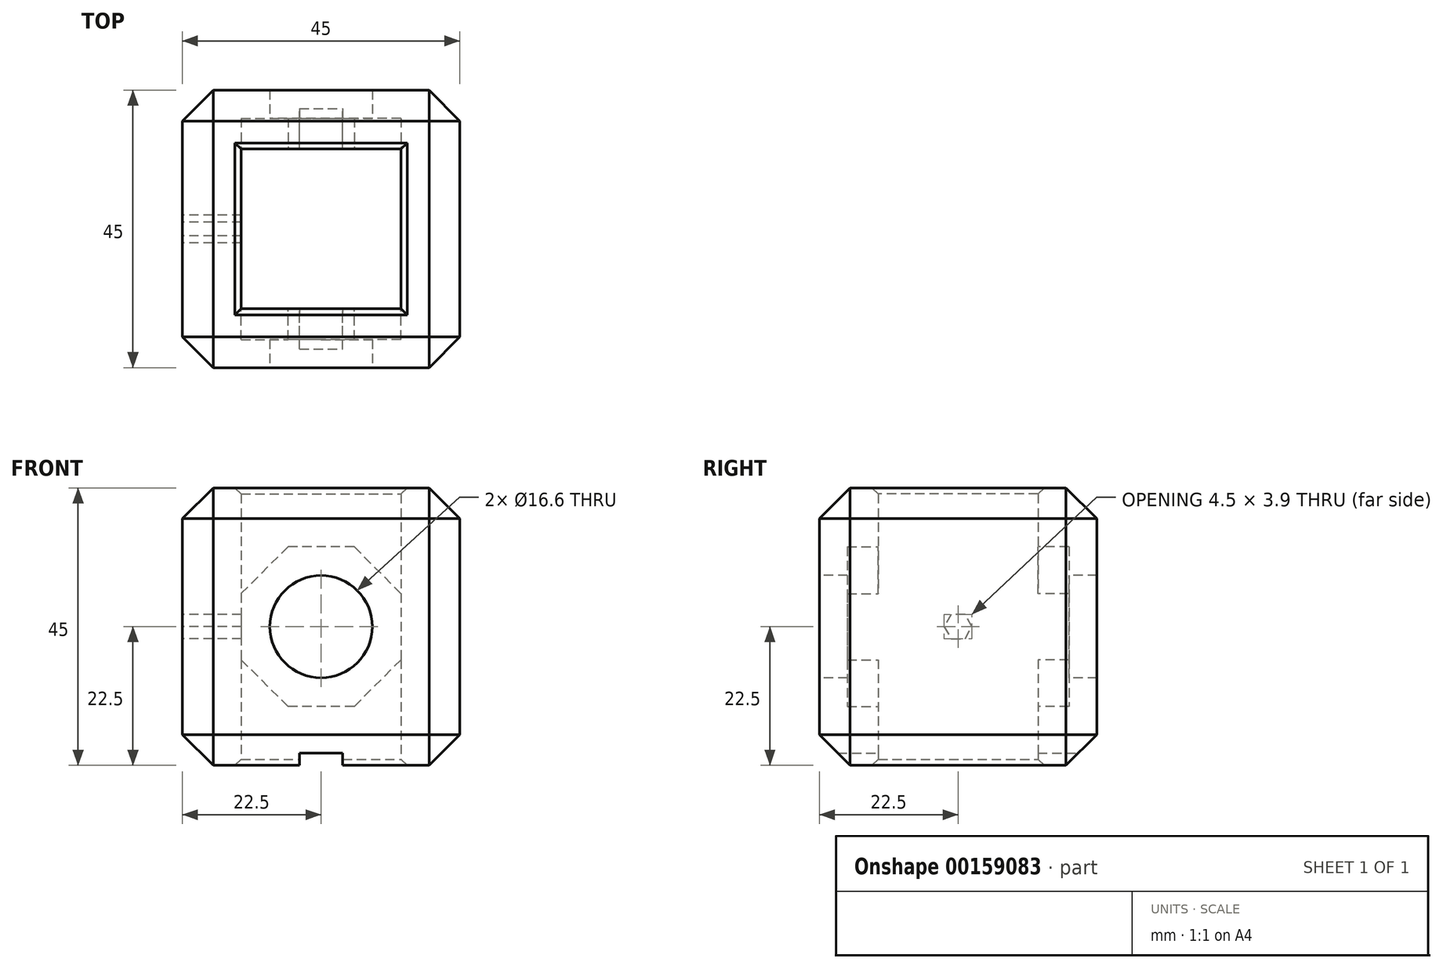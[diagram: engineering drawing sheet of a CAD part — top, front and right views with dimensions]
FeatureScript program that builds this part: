
annotation { "Feature Type Name" : "Feature", "Feature Type Description" : "" }
export const myFeature = defineFeature(function(context is Context, id is Id, definition is map)
    precondition{}
    {
        {
            var Q0;
            Q0=qCreatedBy(makeId("Top.planeOp"),FACE);
            var sketch = newSketch(context, id + "F0", { "sketchPlane" : qUnion([Q0])});
            skLineSegment(sketch, "E0.bottom", {"start": v(12.95, 12.95) * mm, "end": v(-12.95, 12.95) * mm});
            skLineSegment(sketch, "E0.top", {"start": v(12.95, -12.95) * mm, "end": v(-12.95, -12.95) * mm});
            skLineSegment(sketch, "E0.left", {"start": v(12.95, 12.95) * mm, "end": v(12.95, -12.95) * mm});
            skLineSegment(sketch, "E0.right", {"start": v(-12.95, 12.95) * mm, "end": v(-12.95, -12.95) * mm});
            skPoint(sketch, "E0.middle", {"position": v(0, 0) * mm});
            skLineSegment(sketch, "E1.bottom", {"start": v(22.5, -22.5) * mm, "end": v(-22.5, -22.5) * mm});
            skLineSegment(sketch, "E1.top", {"start": v(22.5, 22.5) * mm, "end": v(-22.5, 22.5) * mm});
            skLineSegment(sketch, "E1.left", {"start": v(22.5, -22.5) * mm, "end": v(22.5, 22.5) * mm});
            skLineSegment(sketch, "E1.right", {"start": v(-22.5, -22.5) * mm, "end": v(-22.5, 22.5) * mm});
            skSolve(sketch);
        }
        {
            var Q0;
            Q0=qSketchRegion(id+"F0",true);
            extrude(context, id + "F1", {"entities" : qUnion([Q0]), "depth" : 45 * mm});
        }
        {
            var Q0;
            Q0=makeQuery(id+"F1.opExtrude","SWEPT_FACE",FACE,{"disambiguationData":[OSD([sQuery(id+"F0.wireOp",EDGE,"E1.bottom")])]});
            var sketch = newSketch(context, id + "F2", { "sketchPlane" : qUnion([Q0])});
            skCircle(sketch, "E2", {"center": v(0, 22.5) * mm, "radius": 8.3 * mm});
            skSolve(sketch);
        }
        {
            var Q0;
            Q0=qSketchRegion(id+"F2",true);
            extrude(context, id + "F3", {"entities" : qUnion([Q0]), "operationType" : NewBodyOperationType.REMOVE, "endBound" : BoundingType.THROUGH_ALL, "oppositeDirection" : true, "depth" : 25 * mm});
        }
        {
            var Q0;
            Q0=makeQuery(id+"F1.opExtrude","SWEPT_FACE",FACE,{"disambiguationData":[OSD([sQuery(id+"F0.wireOp",EDGE,"E0.bottom")])]});
            var sketch = newSketch(context, id + "F4", { "sketchPlane" : qUnion([Q0])});
            skCircle(sketch, "E3.cCircle", {"center": v(0, 22.5) * mm, "radius": 12.95 * mm, "construction": true});
            skLineSegment(sketch, "E3.0", {"start": v(12.95, 27.86) * mm, "end": v(12.95, 17.14) * mm});
            skLineSegment(sketch, "E3.1", {"start": v(12.95, 17.14) * mm, "end": v(5.36, 9.55) * mm});
            skLineSegment(sketch, "E3.2", {"start": v(5.36, 9.55) * mm, "end": v(-5.36, 9.55) * mm});
            skLineSegment(sketch, "E3.3", {"start": v(-5.36, 9.55) * mm, "end": v(-12.95, 17.14) * mm});
            skLineSegment(sketch, "E3.4", {"start": v(-12.95, 17.14) * mm, "end": v(-12.95, 27.86) * mm});
            skLineSegment(sketch, "E3.5", {"start": v(-12.95, 27.86) * mm, "end": v(-5.36, 35.45) * mm});
            skLineSegment(sketch, "E3.6", {"start": v(-5.36, 35.45) * mm, "end": v(5.36, 35.45) * mm});
            skLineSegment(sketch, "E3.7", {"start": v(5.36, 35.45) * mm, "end": v(12.95, 27.86) * mm});
            skPoint(sketch, "E3.0.midPoint", {"position": v(12.95, 22.5) * mm});
            skSolve(sketch);
        }
        {
            var Q0;
            Q0=qSketchRegion(id+"F4",true);
            extrude(context, id + "F5", {"entities" : qUnion([Q0]), "operationType" : NewBodyOperationType.REMOVE, "oppositeDirection" : true, "depth" : 5 * mm});
        }
        {
            var Q0;
            Q0=makeQuery(id+"F1.opExtrude","SWEPT_FACE",FACE,{"disambiguationData":[OSD([sQuery(id+"F0.wireOp",EDGE,"E0.top")])]});
            var sketch = newSketch(context, id + "F6", { "sketchPlane" : qUnion([Q0])});
            skCircle(sketch, "E4.cCircle", {"center": v(0, 22.5) * mm, "radius": 12.95 * mm, "construction": true});
            skLineSegment(sketch, "E4.0", {"start": v(12.95, 27.86) * mm, "end": v(12.95, 17.14) * mm});
            skLineSegment(sketch, "E4.1", {"start": v(12.95, 17.14) * mm, "end": v(5.36, 9.55) * mm});
            skLineSegment(sketch, "E4.2", {"start": v(5.36, 9.55) * mm, "end": v(-5.36, 9.55) * mm});
            skLineSegment(sketch, "E4.3", {"start": v(-5.36, 9.55) * mm, "end": v(-12.95, 17.14) * mm});
            skLineSegment(sketch, "E4.4", {"start": v(-12.95, 17.14) * mm, "end": v(-12.95, 27.86) * mm});
            skLineSegment(sketch, "E4.5", {"start": v(-12.95, 27.86) * mm, "end": v(-5.36, 35.45) * mm});
            skLineSegment(sketch, "E4.6", {"start": v(-5.36, 35.45) * mm, "end": v(5.36, 35.45) * mm});
            skLineSegment(sketch, "E4.7", {"start": v(5.36, 35.45) * mm, "end": v(12.95, 27.86) * mm});
            skPoint(sketch, "E4.0.midPoint", {"position": v(12.95, 22.5) * mm});
            skSolve(sketch);
        }
        {
            var Q0;
            Q0=qSketchRegion(id+"F6",true);
            extrude(context, id + "F7", {"entities" : qUnion([Q0]), "operationType" : NewBodyOperationType.REMOVE, "oppositeDirection" : true, "depth" : 5 * mm});
        }
        {
            var Q0;
            Q0=makeQuery(id+"F1.opExtrude","SWEPT_FACE",FACE,{"disambiguationData":[OSD([sQuery(id+"F0.wireOp",EDGE,"E1.right")])]});
            var sketch = newSketch(context, id + "F8", { "sketchPlane" : qUnion([Q0])});
            skLineSegment(sketch, "E5", {"start": v(0, 45) * mm, "end": v(0, 0) * mm, "construction": true});
            skCircle(sketch, "E6.cCircle", {"center": v(0, 22.5) * mm, "radius": 1.95 * mm, "construction": true});
            skLineSegment(sketch, "E6.0", {"start": v(2.25, 22.5) * mm, "end": v(1.13, 20.55) * mm});
            skLineSegment(sketch, "E6.1", {"start": v(1.13, 20.55) * mm, "end": v(-1.13, 20.55) * mm});
            skLineSegment(sketch, "E6.2", {"start": v(-1.13, 20.55) * mm, "end": v(-2.25, 22.5) * mm});
            skLineSegment(sketch, "E6.3", {"start": v(-2.25, 22.5) * mm, "end": v(-1.13, 24.45) * mm});
            skLineSegment(sketch, "E6.4", {"start": v(-1.13, 24.45) * mm, "end": v(1.13, 24.45) * mm});
            skLineSegment(sketch, "E6.5", {"start": v(1.13, 24.45) * mm, "end": v(2.25, 22.5) * mm});
            skPoint(sketch, "E6.0.midPoint", {"position": v(1.69, 21.52) * mm});
            skSolve(sketch);
        }
        {
            var Q0;
            Q0=makeQuery(id+"F1.opExtrude","SWEPT_FACE",FACE,{"disambiguationData":[OSD([sQuery(id+"F0.wireOp",EDGE,"E1.left")])]});
            var Q1;
            Q1=makeQuery(id+"F1.opExtrude","SWEPT_FACE",FACE,{"disambiguationData":[OSD([sQuery(id+"F0.wireOp",EDGE,"E1.right")])]});
            var Q2;
            Q2=makeQuery(id+"F1.opExtrude","CAP_EDGE",EDGE,{"disambiguationData":[OSD([sQuery(id+"F0.wireOp",EDGE,"E1.bottom")])],"isStart":true});
            var Q3;
            Q3=makeQuery(id+"F1.opExtrude","CAP_EDGE",EDGE,{"disambiguationData":[OSD([sQuery(id+"F0.wireOp",EDGE,"E1.bottom")])],"isStart":false});
            var Q4;
            Q4=makeQuery(id+"F1.opExtrude","CAP_EDGE",EDGE,{"disambiguationData":[OSD([sQuery(id+"F0.wireOp",EDGE,"E1.top")])],"isStart":false});
            var Q5;
            Q5=makeQuery(id+"F1.opExtrude","CAP_EDGE",EDGE,{"disambiguationData":[OSD([sQuery(id+"F0.wireOp",EDGE,"E1.top")])],"isStart":true});
            chamfer(context, id + "F9", {"entities" : qUnion([Q0, Q1, Q2, Q3, Q4, Q5]), "width" : 5 * mm, "tangentPropagation" : true});
        }
        {
            var Q0;
            Q0 = qSketchRegion(id + "F8", true);
            extrude(context, id + "F10", {"entities" : qUnion([Q0]), "operationType" : NewBodyOperationType.REMOVE, "endBound" : BoundingType.UP_TO_NEXT, "oppositeDirection" : true, "depth" : 25 * mm});
        }
        {
            var Q0;
            Q0=makeQuery(id+"F5.boolean.opBoolean","INTERSECT",EDGE,{"derivedFrom":[makeQuery(id+"F3.boolean.opBoolean","COPY",FACE,{"disambiguationData":[TD([makeQuery(id+"F1.opExtrude","SWEPT_FACE",FACE,{"disambiguationData":[OSD([sQuery(id+"F0.wireOp",EDGE,"E0.bottom")])]})])],"derivedFrom":makeQuery(id+"F3.opExtrude","SWEPT_FACE",FACE,{"disambiguationData":[OSD([sQuery(id+"F2.wireOp",EDGE,"m8d59r63-g8hb-ZFIC-Y3uv-W7ZignHRoER8")])]})}),makeQuery(id+"F5.opExtrude","CAP_FACE",FACE,{"disambiguationData":[OSD([sQuery(id+"F4.wireOp",EDGE,"4a96c423-e548-48cd-aa36-1517ae86cc45.0")])],"isStart":false})]});
            var Q1;
            Q1=makeQuery(id+"F7.boolean.opBoolean","INTERSECT",EDGE,{"derivedFrom":[makeQuery(id+"F3.boolean.opBoolean","COPY",FACE,{"disambiguationData":[TD([makeQuery(id+"F1.opExtrude","SWEPT_FACE",FACE,{"disambiguationData":[OSD([sQuery(id+"F0.wireOp",EDGE,"E0.top")])]})])],"derivedFrom":makeQuery(id+"F3.opExtrude","SWEPT_FACE",FACE,{"disambiguationData":[OSD([sQuery(id+"F2.wireOp",EDGE,"m8d59r63-g8hb-ZFIC-Y3uv-W7ZignHRoER8")])]})}),makeQuery(id+"F7.opExtrude","CAP_FACE",FACE,{"disambiguationData":[OSD([sQuery(id+"F6.wireOp",EDGE,"4c9e81c7-f19d-4fb6-93af-8531212ddbce.0")])],"isStart":false})]});
            var Q2;
            Q2=makeQuery(id+"F1.opExtrude","CAP_EDGE",EDGE,{"disambiguationData":[OSD([sQuery(id+"F0.wireOp",EDGE,"E0.left")])],"isStart":false});
            var Q3;
            Q3=makeQuery(id+"F1.opExtrude","CAP_EDGE",EDGE,{"disambiguationData":[OSD([sQuery(id+"F0.wireOp",EDGE,"E0.top")])],"isStart":false});
            var Q4;
            Q4=makeQuery(id+"F1.opExtrude","CAP_EDGE",EDGE,{"disambiguationData":[OSD([sQuery(id+"F0.wireOp",EDGE,"E0.right")])],"isStart":false});
            var Q5;
            Q5=makeQuery(id+"F1.opExtrude","CAP_EDGE",EDGE,{"disambiguationData":[OSD([sQuery(id+"F0.wireOp",EDGE,"E0.bottom")])],"isStart":false});
            var Q6;
            Q6=makeQuery(id+"F1.opExtrude","CAP_EDGE",EDGE,{"disambiguationData":[OSD([sQuery(id+"F0.wireOp",EDGE,"E0.right")])],"isStart":true});
            var Q7;
            Q7=makeQuery(id+"F1.opExtrude","CAP_EDGE",EDGE,{"disambiguationData":[OSD([sQuery(id+"F0.wireOp",EDGE,"E0.bottom")])],"isStart":true});
            var Q8;
            Q8=makeQuery(id+"F1.opExtrude","CAP_EDGE",EDGE,{"disambiguationData":[OSD([sQuery(id+"F0.wireOp",EDGE,"E0.left")])],"isStart":true});
            var Q9;
            Q9=makeQuery(id+"F1.opExtrude","CAP_EDGE",EDGE,{"disambiguationData":[OSD([sQuery(id+"F0.wireOp",EDGE,"E0.top")])],"isStart":true});
            chamfer(context, id + "F11", {"entities" : qUnion([Q0, Q1, Q2, Q3, Q4, Q5, Q6, Q7, Q8, Q9]), "width" : 1 * mm, "tangentPropagation" : true});
        }
        {
            var Q0;
            Q0=makeQuery(id+"F1.opExtrude","CAP_FACE",FACE,{"disambiguationData":[OSD([sQuery(id+"F0.wireOp",EDGE,"E0.bottom"),sQuery(id+"F0.wireOp",EDGE,"E0.top"),sQuery(id+"F0.wireOp",EDGE,"E0.left"),sQuery(id+"F0.wireOp",EDGE,"E0.right"),sQuery(id+"F0.wireOp",EDGE,"E1.bottom"),sQuery(id+"F0.wireOp",EDGE,"E1.top"),sQuery(id+"F0.wireOp",EDGE,"E1.left"),sQuery(id+"F0.wireOp",EDGE,"E1.right")])],"isStart":true});
            var sketch = newSketch(context, id + "F12", { "sketchPlane" : qUnion([Q0])});
            skLineSegment(sketch, "E7.bottom", {"start": v(3.5, 30) * mm, "end": v(-3.5, 30) * mm});
            skLineSegment(sketch, "E7.top", {"start": v(3.5, -30) * mm, "end": v(-3.5, -30) * mm});
            skLineSegment(sketch, "E7.left", {"start": v(3.5, 30) * mm, "end": v(3.5, -30) * mm});
            skLineSegment(sketch, "E7.right", {"start": v(-3.5, 30) * mm, "end": v(-3.5, -30) * mm});
            skPoint(sketch, "E7.middle", {"position": v(0, 0) * mm});
            skSolve(sketch);
        }
        {
            var Q0;
            Q0 = qSketchRegion(id + "F12", true);
            extrude(context, id + "F13", {"entities" : qUnion([Q0]), "operationType" : NewBodyOperationType.REMOVE, "oppositeDirection" : true, "depth" : 2 * mm});
        }
    });
